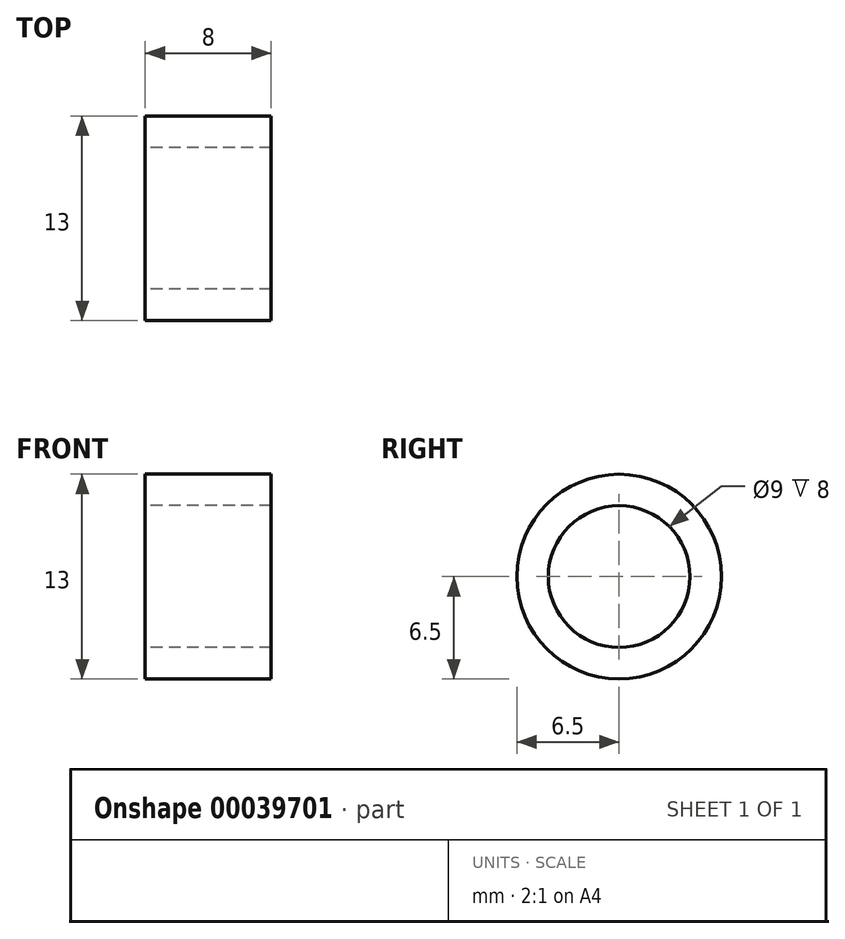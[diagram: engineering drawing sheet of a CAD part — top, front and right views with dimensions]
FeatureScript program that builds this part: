
annotation { "Feature Type Name" : "Feature", "Feature Type Description" : "" }
export const myFeature = defineFeature(function(context is Context, id is Id, definition is map)
    precondition{}
    {
        {
            var Q0;
            Q0=qCreatedBy(makeId("Right.planeOp"),FACE);
            var sketch = newSketch(context, id + "F0", { "sketchPlane" : qUnion([Q0])});
            skCircle(sketch, "E0", {"center": v(0, 0) * mm, "radius": 4.5 * mm});
            skCircle(sketch, "E1", {"center": v(0, 0) * mm, "radius": 6.5 * mm});
            skSolve(sketch);
        }
        {
            var Q0;
            Q0=makeQuery(id+"F0.imprint","IMPRINT",FACE,{"disambiguationData":[TD([[makeQuery(id+"F0.imprint","IMPRINT",EDGE,{"derivedFrom":sQuery(id+"F0.wireOp",EDGE,"E0")}),-1.0]])]});
            extrude(context, id + "F1", {"entities" : qUnion([Q0]), "depth" : 8 * mm});
        }
    });
